# Revit family: Sofiero-Bar-Table-CC
name_source: partatom
category: Furniture
units: mm (PartAtom-declared; Revit-internal decimal feet)

## family parameters
Always vertical = Yes
Cut with Voids When Loaded = No
OmniClass Number = 23.21.23.13.15
Room Calculation Point = No
Shared = No
Work Plane-Based = No

## types (4) — shared parameters
BIMobject category = Tables
Description = Bar table Sofiero Cast
Edition number = 1
IFC Classification = Furniture
Manufacturer = Hags
Manufacturer name = HAGS
OmniClass Code = 23-11 29 15
OmniClass Description = Exterior Tables
Product Guid = 74a7f8cc-50c8-4232-b650-bed65a17cf03
Product SKU = Bar_table_Sofiero_Cast
Product data url = https://bimobject.com
Product name = Sofiero Bar table
QR code = https://bimobject.com
URL = https://www.hags.com
Uniclass 1.4 Code = JN
Uniclass 1.4 Description = Furniture/Equipment
zero-valued in all types: Default Elevation

## per-type parameters (varying)
| type | Body material | Body material_90 | Construction material | Model | Product url |
| 8077418 Bark Brown / Black | Hags - Wood - Bark brown | Hags - Wood - Bark brown 90 | Hags - Steel - Powder coated - Black | 8077418 | https://hags.se |
| 8077425 Tan / Galvanized | Hags - Wood - Tan | Hags - Wood - Tan 90 | Hags - Steel - Galvanized | 8077425 | https://hags.se |
| 8097646 Hardwood / Galvanized | Hags - Hard Wood | Hags - Hard Wood | Hags - Steel - Galvanized | 8097646 | https://www.hags.com |
| 8097647 Hardwood / Black | Hags - Hard Wood | Hags - Hard Wood | Hags - Steel - Galvanized | 8097647 | https://www.hags.com |

## geometry (parser evidence)
native form markers: Sweep x5
no freeform markers — native parametric forms only
